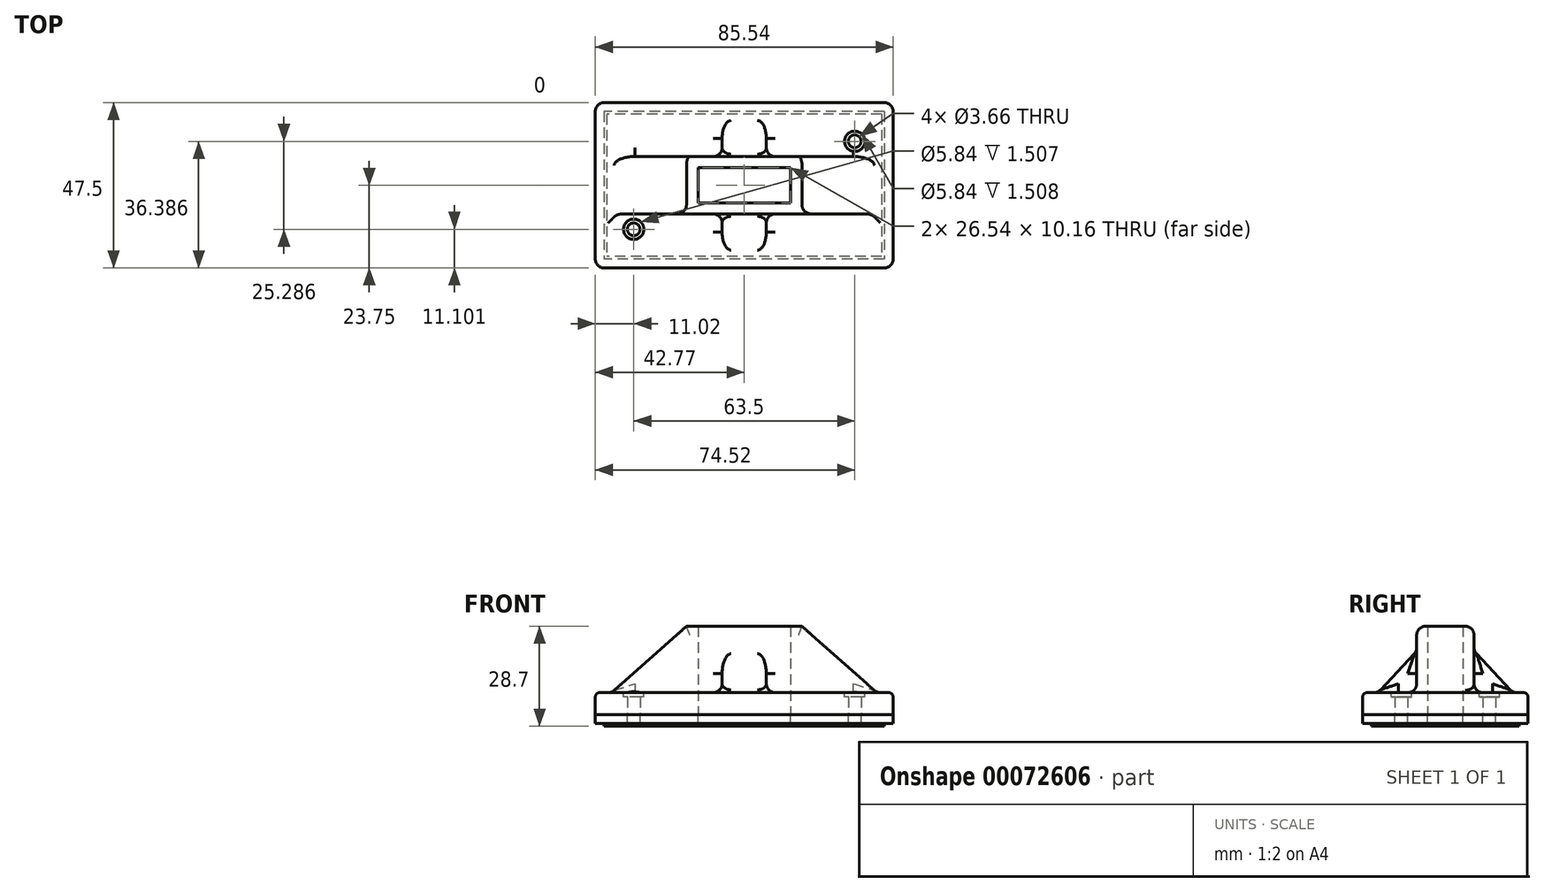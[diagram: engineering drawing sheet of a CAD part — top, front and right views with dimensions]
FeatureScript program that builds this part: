
annotation { "Feature Type Name" : "Feature", "Feature Type Description" : "" }
export const myFeature = defineFeature(function(context is Context, id is Id, definition is map)
    precondition{}
    {
        {
            var Q0;
            Q0=qCreatedBy(makeId("Top.planeOp"),FACE);
            var sketch = newSketch(context, id + "F0", { "sketchPlane" : qUnion([Q0])});
            skLineSegment(sketch, "E0.rect.bottom", {"start": v(42.77, 23.75) * mm, "end": v(-42.77, 23.75) * mm});
            skLineSegment(sketch, "E0.rect.top", {"start": v(42.77, -23.75) * mm, "end": v(-42.77, -23.75) * mm});
            skLineSegment(sketch, "E0.rect.left", {"start": v(42.77, 23.75) * mm, "end": v(42.77, -23.75) * mm});
            skLineSegment(sketch, "E0.rect.right", {"start": v(-42.77, 23.75) * mm, "end": v(-42.77, -23.75) * mm});
            skPoint(sketch, "E0.rect.middle", {"position": v(0, 0) * mm});
            skCircle(sketch, "E1", {"center": v(31.75, 12.64) * mm, "radius": 1.83 * mm});
            skCircle(sketch, "E2", {"center": v(-31.75, -12.65) * mm, "radius": 1.83 * mm});
            skSolve(sketch);
        }
        {
            var Q0;
            Q0 = qSketchRegion(id + "F0", true);
            extrude(context, id + "F1", {"entities" : qUnion([Q0]), "depth" : 6.35 * mm});
        }
        {
            var Q0;
            Q0=qCreatedBy(makeId("Top.planeOp"),FACE);
            var sketch = newSketch(context, id + "F2", { "sketchPlane" : qUnion([Q0])});
            skLineSegment(sketch, "E3.rect.bottom", {"start": v(38.1, -8.26) * mm, "end": v(-38.1, -8.26) * mm});
            skLineSegment(sketch, "E3.rect.top", {"start": v(38.1, 8.26) * mm, "end": v(-38.1, 8.26) * mm});
            skLineSegment(sketch, "E3.rect.left", {"start": v(38.1, -8.26) * mm, "end": v(38.1, 8.25) * mm});
            skLineSegment(sketch, "E3.rect.right", {"start": v(-38.1, -8.26) * mm, "end": v(-38.1, 8.25) * mm});
            skPoint(sketch, "E3.rect.middle", {"position": v(0, 0) * mm});
            skLineSegment(sketch, "E4.rect.bottom", {"start": v(13.27, -5.08) * mm, "end": v(-13.27, -5.08) * mm});
            skLineSegment(sketch, "E4.rect.top", {"start": v(13.27, 5.08) * mm, "end": v(-13.27, 5.08) * mm});
            skLineSegment(sketch, "E4.rect.left", {"start": v(13.27, -5.08) * mm, "end": v(13.27, 5.08) * mm});
            skLineSegment(sketch, "E4.rect.right", {"start": v(-13.27, -5.08) * mm, "end": v(-13.27, 5.08) * mm});
            skSolve(sketch);
        }
        {
            var Q0;
            Q0 = qSketchRegion(id + "F2", true);
            extrude(context, id + "F3", {"entities" : qUnion([Q0]), "operationType" : NewBodyOperationType.ADD, "depth" : 25.4 * mm});
        }
        {
            var Q0;
            Q0=makeQuery(id+"F3.opExtrude","SWEPT_FACE",FACE,{"disambiguationData":[OSD([sQuery(id+"F2.wireOp",EDGE,"E3.rect.bottom")])]});
            var sketch = newSketch(context, id + "F4", { "sketchPlane" : qUnion([Q0])});
            skPoint(sketch, "E5", {"position": v(16.6, 25.4) * mm});
            skPoint(sketch, "E6", {"position": v(-16.6, 25.4) * mm});
            skLineSegment(sketch, "E7", {"start": v(16.6, 25.4) * mm, "end": v(38.1, 6.35) * mm});
            skLineSegment(sketch, "E8", {"start": v(-16.6, 25.4) * mm, "end": v(-38.1, 6.35) * mm});
            skLineSegment(sketch, "E9", {"start": v(-16.6, 25.4) * mm, "end": v(16.6, 25.4) * mm});
            skLineSegment(sketch, "E10", {"start": v(38.1, 6.35) * mm, "end": v(-38.1, 6.35) * mm});
            skSolve(sketch);
        }
        {
            var Q0;
            {var subQ0=sQuery(id+"F4.wireOp",EDGE,"E7");Q0=makeQuery(id+"F4.imprint","IMPRINT",FACE,{"disambiguationData":[TD([[makeQuery(id+"F4.imprint","IMPRINT",EDGE,{"derivedFrom":subQ0}),1.0]])]});}
            extrude(context, id + "F5", {"entities" : qUnion([Q0]), "operationType" : NewBodyOperationType.REMOVE, "oppositeDirection" : true, "depth" : 44.81 * mm});
        }
        {
            var Q0;
            {var subQ0=sQuery(id+"F4.wireOp",EDGE,"E8");Q0=makeQuery(id+"F4.imprint","IMPRINT",FACE,{"disambiguationData":[TD([[makeQuery(id+"F4.imprint","IMPRINT",EDGE,{"derivedFrom":subQ0}),-1.0]])]});}
            extrude(context, id + "F6", {"entities" : qUnion([Q0]), "operationType" : NewBodyOperationType.REMOVE, "oppositeDirection" : true, "depth" : 25.4 * mm});
        }
        {
            var Q0;
            Q0=makeQuery(id+"F3.opExtrude","CAP_EDGE",EDGE,{"disambiguationData":[OSD([sQuery(id+"F2.wireOp",EDGE,"E3.rect.bottom")])],"isStart":false});
            var Q1;
            Q1=makeQuery(id+"F6.boolean.opBoolean","COPY",EDGE,{"derivedFrom":makeQuery(id+"F6.opExtrude","SWEPT_EDGE",EDGE,{"disambiguationData":[OSD([sQuery(id+"F2.wireOp",EDGE,"E3.rect.bottom"),sQuery(id+"F4.wireOp",EDGE,"E8"),sQuery(id+"F4.wireOp",EDGE,"E9")])]})});
            var Q2;
            Q2=makeQuery(id+"F3.opExtrude","CAP_EDGE",EDGE,{"disambiguationData":[OSD([sQuery(id+"F2.wireOp",EDGE,"E3.rect.top")])],"isStart":false});
            var Q3;
            Q3=makeQuery(id+"F5.boolean.opBoolean","COPY",EDGE,{"derivedFrom":makeQuery(id+"F5.opExtrude","SWEPT_EDGE",EDGE,{"disambiguationData":[OSD([sQuery(id+"F2.wireOp",EDGE,"E3.rect.bottom"),sQuery(id+"F4.wireOp",EDGE,"E7"),sQuery(id+"F4.wireOp",EDGE,"E9")])]})});
            var Q4;
            Q4=makeQuery(id+"F5.boolean.opBoolean","COPY",EDGE,{"derivedFrom":makeQuery(id+"F5.opExtrude","CAP_EDGE",EDGE,{"disambiguationData":[OSD([sQuery(id+"F4.wireOp",EDGE,"E7")])],"isStart":true})});
            var Q5;
            Q5=makeQuery(id+"F5.boolean.opBoolean","INTERSECT",EDGE,{"derivedFrom":[makeQuery(id+"F3.opExtrude","SWEPT_FACE",FACE,{"disambiguationData":[OSD([sQuery(id+"F2.wireOp",EDGE,"E3.rect.top")])]}),makeQuery(id+"F5.opExtrude","SWEPT_FACE",FACE,{"disambiguationData":[OSD([sQuery(id+"F4.wireOp",EDGE,"E7")])]})]});
            var Q6;
            Q6=makeQuery(id+"F6.boolean.opBoolean","COPY",EDGE,{"derivedFrom":makeQuery(id+"F6.opExtrude","CAP_EDGE",EDGE,{"disambiguationData":[OSD([sQuery(id+"F4.wireOp",EDGE,"E8")])],"isStart":true})});
            var Q7;
            Q7=makeQuery(id+"F6.boolean.opBoolean","INTERSECT",EDGE,{"derivedFrom":[makeQuery(id+"F3.opExtrude","SWEPT_FACE",FACE,{"disambiguationData":[OSD([sQuery(id+"F2.wireOp",EDGE,"E3.rect.top")])]}),makeQuery(id+"F6.opExtrude","SWEPT_FACE",FACE,{"disambiguationData":[OSD([sQuery(id+"F4.wireOp",EDGE,"E8")])]})]});
            var Q8;
            Q8=makeQuery(id+"F3.boolean.opBoolean","INTERSECT",EDGE,{"derivedFrom":[makeQuery(id+"F1.opExtrude","CAP_FACE",FACE,{"disambiguationData":[OSD([sQuery(id+"F0.wireOp",EDGE,"E0.rect.bottom"),sQuery(id+"F0.wireOp",EDGE,"E0.rect.top"),sQuery(id+"F0.wireOp",EDGE,"E0.rect.left"),sQuery(id+"F0.wireOp",EDGE,"E0.rect.right"),sQuery(id+"F0.wireOp",EDGE,"E1"),sQuery(id+"F0.wireOp",EDGE,"E2")])],"isStart":false}),makeQuery(id+"F3.opExtrude","SWEPT_FACE",FACE,{"disambiguationData":[OSD([sQuery(id+"F2.wireOp",EDGE,"E3.rect.bottom")])]})]});
            var Q9;
            Q9=makeQuery(id+"F3.boolean.opBoolean","INTERSECT",EDGE,{"derivedFrom":[makeQuery(id+"F1.opExtrude","CAP_FACE",FACE,{"disambiguationData":[OSD([sQuery(id+"F0.wireOp",EDGE,"E0.rect.bottom"),sQuery(id+"F0.wireOp",EDGE,"E0.rect.top"),sQuery(id+"F0.wireOp",EDGE,"E0.rect.left"),sQuery(id+"F0.wireOp",EDGE,"E0.rect.right"),sQuery(id+"F0.wireOp",EDGE,"E1"),sQuery(id+"F0.wireOp",EDGE,"E2")])],"isStart":false}),makeQuery(id+"F3.opExtrude","SWEPT_FACE",FACE,{"disambiguationData":[OSD([sQuery(id+"F2.wireOp",EDGE,"E3.rect.top")])]})]});
            var Q10;
            {var subQ0=sQuery(id+"F2.wireOp",EDGE,"E3.rect.right");Q10=makeQuery(id+"F6.boolean.opBoolean","MERGE",EDGE,{"derivedFrom":[makeQuery(id+"F3.boolean.opBoolean","INTERSECT",EDGE,{"derivedFrom":[makeQuery(id+"F1.opExtrude","CAP_FACE",FACE,{"disambiguationData":[OSD([sQuery(id+"F0.wireOp",EDGE,"E0.rect.bottom"),sQuery(id+"F0.wireOp",EDGE,"E0.rect.top"),sQuery(id+"F0.wireOp",EDGE,"E0.rect.left"),sQuery(id+"F0.wireOp",EDGE,"E0.rect.right"),sQuery(id+"F0.wireOp",EDGE,"E1"),sQuery(id+"F0.wireOp",EDGE,"E2")])],"isStart":false}),makeQuery(id+"F3.opExtrude","SWEPT_FACE",FACE,{"disambiguationData":[OSD([subQ0])]})]}),makeQuery(id+"F6.opExtrude","SWEPT_EDGE",EDGE,{"disambiguationData":[OSD([sQuery(id+"F2.wireOp",EDGE,"E3.rect.bottom"),subQ0,sQuery(id+"F4.wireOp",EDGE,"E8"),sQuery(id+"F4.wireOp",EDGE,"E10")])]})]});}
            var Q11;
            {var subQ0=sQuery(id+"F2.wireOp",EDGE,"E3.rect.left");Q11=makeQuery(id+"F5.boolean.opBoolean","MERGE",EDGE,{"derivedFrom":[makeQuery(id+"F3.boolean.opBoolean","INTERSECT",EDGE,{"derivedFrom":[makeQuery(id+"F1.opExtrude","CAP_FACE",FACE,{"disambiguationData":[OSD([sQuery(id+"F0.wireOp",EDGE,"E0.rect.bottom"),sQuery(id+"F0.wireOp",EDGE,"E0.rect.top"),sQuery(id+"F0.wireOp",EDGE,"E0.rect.left"),sQuery(id+"F0.wireOp",EDGE,"E0.rect.right"),sQuery(id+"F0.wireOp",EDGE,"E1"),sQuery(id+"F0.wireOp",EDGE,"E2")])],"isStart":false}),makeQuery(id+"F3.opExtrude","SWEPT_FACE",FACE,{"disambiguationData":[OSD([subQ0])]})]}),makeQuery(id+"F5.opExtrude","SWEPT_EDGE",EDGE,{"disambiguationData":[OSD([sQuery(id+"F2.wireOp",EDGE,"E3.rect.bottom"),subQ0,sQuery(id+"F4.wireOp",EDGE,"E7"),sQuery(id+"F4.wireOp",EDGE,"E10")])]})]});}
            fillet(context, id + "F7", {"entities" : qUnion([Q0, Q1, Q2, Q3, Q4, Q5, Q6, Q7, Q8, Q9, Q10, Q11]), "radius" : 2.54 * mm, "tangentPropagation" : true, "allowEdgeOverflow" : false});
        }
        {
            var Q0;
            Q0=makeQuery(id+"F1.opExtrude","CAP_EDGE",EDGE,{"disambiguationData":[OSD([sQuery(id+"F0.wireOp",EDGE,"E0.rect.top")])],"isStart":false});
            var Q1;
            Q1=makeQuery(id+"F1.opExtrude","CAP_EDGE",EDGE,{"disambiguationData":[OSD([sQuery(id+"F0.wireOp",EDGE,"E0.rect.right")])],"isStart":false});
            var Q2;
            Q2=makeQuery(id+"F1.opExtrude","CAP_EDGE",EDGE,{"disambiguationData":[OSD([sQuery(id+"F0.wireOp",EDGE,"E0.rect.bottom")])],"isStart":false});
            var Q3;
            Q3=makeQuery(id+"F1.opExtrude","CAP_EDGE",EDGE,{"disambiguationData":[OSD([sQuery(id+"F0.wireOp",EDGE,"E0.rect.left")])],"isStart":false});
            fillet(context, id + "F8", {"entities" : qUnion([Q0, Q1, Q2, Q3]), "radius" : 1.27 * mm, "tangentPropagation" : true, "allowEdgeOverflow" : false});
        }
        {
            var Q0;
            Q0=makeQuery(id+"F1.opExtrude","SWEPT_EDGE",EDGE,{"disambiguationData":[OSD([sQuery(id+"F0.wireOp",EDGE,"E0.rect.bottom"),sQuery(id+"F0.wireOp",EDGE,"E0.rect.left")])]});
            var Q1;
            Q1=makeQuery(id+"F1.opExtrude","SWEPT_EDGE",EDGE,{"disambiguationData":[OSD([sQuery(id+"F0.wireOp",EDGE,"E0.rect.bottom"),sQuery(id+"F0.wireOp",EDGE,"E0.rect.right")])]});
            var Q2;
            Q2=makeQuery(id+"F1.opExtrude","SWEPT_EDGE",EDGE,{"disambiguationData":[OSD([sQuery(id+"F0.wireOp",EDGE,"E0.rect.top"),sQuery(id+"F0.wireOp",EDGE,"E0.rect.right")])]});
            var Q3;
            Q3=makeQuery(id+"F1.opExtrude","SWEPT_EDGE",EDGE,{"disambiguationData":[OSD([sQuery(id+"F0.wireOp",EDGE,"E0.rect.top"),sQuery(id+"F0.wireOp",EDGE,"E0.rect.left")])]});
            fillet(context, id + "F9", {"entities" : qUnion([Q0, Q1, Q2, Q3]), "radius" : 2.54 * mm, "tangentPropagation" : true, "allowEdgeOverflow" : false});
        }
        {
            var Q0;
            {var subQ0=sQuery(id+"F0.wireOp",EDGE,"E0.rect.right");var subQ1=sQuery(id+"F0.wireOp",EDGE,"E0.rect.left");var subQ2=sQuery(id+"F0.wireOp",EDGE,"E0.rect.top");var subQ3=sQuery(id+"F0.wireOp",EDGE,"E0.rect.bottom");var subQ4=sQuery(id+"F0.wireOp",EDGE,"E1");var subQ5=sQuery(id+"F0.wireOp",EDGE,"E2");Q0=makeQuery(id+"F3.boolean.opBoolean","SPLIT",FACE,{"disambiguationData":[TD([makeQuery(id+"F1.opExtrude","SWEPT_FACE",FACE,{"disambiguationData":[OSD([subQ3])]})])],"derivedFrom":makeQuery(id+"F1.opExtrude","CAP_FACE",FACE,{"disambiguationData":[OSD([subQ3,subQ2,subQ1,subQ0,subQ4,subQ5])],"isStart":false})});}
            var sketch = newSketch(context, id + "F10", { "sketchPlane" : qUnion([Q0])});
            skCircle(sketch, "E11", {"center": v(31.75, 12.64) * mm, "radius": 2.92 * mm});
            skCircle(sketch, "E12", {"center": v(-31.75, -12.65) * mm, "radius": 2.92 * mm});
            skSolve(sketch);
        }
        {
            var Q0;
            Q0 = qSketchRegion(id + "F10", true);
            extrude(context, id + "F11", {"entities" : qUnion([Q0]), "operationType" : NewBodyOperationType.REMOVE, "endBound" : BoundingType.SYMMETRIC, "oppositeDirection" : true, "depth" : 2.54 * mm});
        }
        {
            var Q0;
            Q0=qCreatedBy(makeId("Top.planeOp"),FACE);
            var sketch = newSketch(context, id + "F12", { "sketchPlane" : qUnion([Q0])});
            skLineSegment(sketch, "E13.rect.bottom", {"start": v(13.27, -5.08) * mm, "end": v(-13.27, -5.08) * mm});
            skLineSegment(sketch, "E13.rect.top", {"start": v(13.27, 5.08) * mm, "end": v(-13.27, 5.08) * mm});
            skLineSegment(sketch, "E13.rect.left", {"start": v(13.27, -5.08) * mm, "end": v(13.27, 5.08) * mm});
            skLineSegment(sketch, "E13.rect.right", {"start": v(-13.27, -5.08) * mm, "end": v(-13.27, 5.08) * mm});
            skPoint(sketch, "E13.rect.middle", {"position": v(0, 0) * mm});
            skSolve(sketch);
        }
        {
            var Q0;
            Q0 = qSketchRegion(id + "F12", true);
            extrude(context, id + "F13", {"entities" : qUnion([Q0]), "operationType" : NewBodyOperationType.REMOVE, "depth" : 25.4 * mm});
        }
        {
            var Q0;
            Q0=qCreatedBy(makeId("Right.planeOp"),FACE);
            var sketch = newSketch(context, id + "F14", { "sketchPlane" : qUnion([Q0])});
            skLineSegment(sketch, "E14", {"start": v(7.87, 18.64) * mm, "end": v(19.7, 6) * mm});
            skLineSegment(sketch, "E15", {"start": v(19.7, 6) * mm, "end": v(7.62, 6) * mm});
            skLineSegment(sketch, "E16", {"start": v(7.62, 6) * mm, "end": v(7.87, 18.64) * mm});
            skLineSegment(sketch, "E17.MirrorCS", {"start": v(-7.87, 18.64) * mm, "end": v(-19.7, 6) * mm});
            skLineSegment(sketch, "E18.MirrorCS", {"start": v(-7.62, 6) * mm, "end": v(-7.87, 18.64) * mm});
            skLineSegment(sketch, "E19.MirrorCS", {"start": v(-19.7, 6) * mm, "end": v(-7.62, 6) * mm});
            skSolve(sketch);
        }
        {
            var Q0;
            Q0 = qSketchRegion(id + "F14", true);
            extrude(context, id + "F15", {"entities" : qUnion([Q0]), "operationType" : NewBodyOperationType.ADD, "endBound" : BoundingType.SYMMETRIC, "depth" : 12.7 * mm});
        }
        {
            var Q0;
            Q0=makeQuery(id+"F15.boolean.opBoolean","INTERSECT",EDGE,{"derivedFrom":[makeQuery(id+"F3.opExtrude","SWEPT_FACE",FACE,{"disambiguationData":[OSD([sQuery(id+"F2.wireOp",EDGE,"E3.rect.bottom")])]}),makeQuery(id+"F15.opExtrude","SWEPT_FACE",FACE,{"disambiguationData":[OSD([sQuery(id+"F14.wireOp",EDGE,"E17.MirrorCS")])]})]});
            var Q1;
            Q1=makeQuery(id+"F15.opExtrude","CAP_EDGE",EDGE,{"disambiguationData":[OSD([sQuery(id+"F14.wireOp",EDGE,"E17.MirrorCS")])],"isStart":true});
            var Q2;
            Q2=makeQuery(id+"F15.opExtrude","CAP_EDGE",EDGE,{"disambiguationData":[OSD([sQuery(id+"F14.wireOp",EDGE,"E17.MirrorCS")])],"isStart":false});
            var Q3;
            {var subQ0=sQuery(id+"F0.wireOp",EDGE,"E0.rect.right");var subQ1=sQuery(id+"F0.wireOp",EDGE,"E0.rect.left");var subQ2=sQuery(id+"F0.wireOp",EDGE,"E0.rect.top");var subQ3=sQuery(id+"F0.wireOp",EDGE,"E0.rect.bottom");var subQ4=sQuery(id+"F0.wireOp",EDGE,"E1");var subQ5=sQuery(id+"F0.wireOp",EDGE,"E2");Q3=makeQuery(id+"F15.boolean.opBoolean","INTERSECT",EDGE,{"derivedFrom":[makeQuery(id+"F3.boolean.opBoolean","SPLIT",FACE,{"disambiguationData":[TD([makeQuery(id+"F1.opExtrude","SWEPT_FACE",FACE,{"disambiguationData":[OSD([subQ3])]})])],"derivedFrom":makeQuery(id+"F1.opExtrude","CAP_FACE",FACE,{"disambiguationData":[OSD([subQ3,subQ2,subQ1,subQ0,subQ4,subQ5])],"isStart":false})}),makeQuery(id+"F15.opExtrude","SWEPT_FACE",FACE,{"disambiguationData":[OSD([sQuery(id+"F14.wireOp",EDGE,"E17.MirrorCS")])]})]});}
            var Q4;
            Q4=makeQuery(id+"F15.opExtrude","CAP_FACE",FACE,{"disambiguationData":[OSD([sQuery(id+"F14.wireOp",EDGE,"E17.MirrorCS"),sQuery(id+"F14.wireOp",EDGE,"E18.MirrorCS"),sQuery(id+"F14.wireOp",EDGE,"E19.MirrorCS")])],"isStart":true});
            var Q5;
            Q5=makeQuery(id+"F15.opExtrude","CAP_FACE",FACE,{"disambiguationData":[OSD([sQuery(id+"F14.wireOp",EDGE,"E17.MirrorCS"),sQuery(id+"F14.wireOp",EDGE,"E18.MirrorCS"),sQuery(id+"F14.wireOp",EDGE,"E19.MirrorCS")])],"isStart":false});
            fillet(context, id + "F16", {"entities" : qUnion([Q0, Q1, Q2, Q3, Q4, Q5]), "radius" : 2.54 * mm, "tangentPropagation" : true, "allowEdgeOverflow" : false});
        }
        {
            var Q0;
            Q0=makeQuery(id+"F15.boolean.opBoolean","INTERSECT",EDGE,{"derivedFrom":[makeQuery(id+"F3.opExtrude","SWEPT_FACE",FACE,{"disambiguationData":[OSD([sQuery(id+"F2.wireOp",EDGE,"E3.rect.top")])]}),makeQuery(id+"F15.opExtrude","SWEPT_FACE",FACE,{"disambiguationData":[OSD([sQuery(id+"F14.wireOp",EDGE,"E14")])]})]});
            var Q1;
            Q1=makeQuery(id+"F15.opExtrude","CAP_EDGE",EDGE,{"disambiguationData":[OSD([sQuery(id+"F14.wireOp",EDGE,"E14")])],"isStart":true});
            var Q2;
            {var subQ0=sQuery(id+"F0.wireOp",EDGE,"E0.rect.right");var subQ1=sQuery(id+"F0.wireOp",EDGE,"E0.rect.left");var subQ2=sQuery(id+"F0.wireOp",EDGE,"E0.rect.top");var subQ3=sQuery(id+"F0.wireOp",EDGE,"E0.rect.bottom");var subQ4=sQuery(id+"F0.wireOp",EDGE,"E1");var subQ5=sQuery(id+"F0.wireOp",EDGE,"E2");Q2=makeQuery(id+"F15.boolean.opBoolean","INTERSECT",EDGE,{"derivedFrom":[makeQuery(id+"F3.boolean.opBoolean","SPLIT",FACE,{"disambiguationData":[TD([makeQuery(id+"F1.opExtrude","SWEPT_FACE",FACE,{"disambiguationData":[OSD([subQ3])]})])],"derivedFrom":makeQuery(id+"F1.opExtrude","CAP_FACE",FACE,{"disambiguationData":[OSD([subQ3,subQ2,subQ1,subQ0,subQ4,subQ5])],"isStart":false})}),makeQuery(id+"F15.opExtrude","SWEPT_FACE",FACE,{"disambiguationData":[OSD([sQuery(id+"F14.wireOp",EDGE,"E14")])]})]});}
            var Q3;
            Q3=makeQuery(id+"F15.opExtrude","CAP_EDGE",EDGE,{"disambiguationData":[OSD([sQuery(id+"F14.wireOp",EDGE,"E14")])],"isStart":false});
            var Q4;
            Q4=makeQuery(id+"F15.opExtrude","CAP_FACE",FACE,{"disambiguationData":[OSD([sQuery(id+"F14.wireOp",EDGE,"E14"),sQuery(id+"F14.wireOp",EDGE,"E15"),sQuery(id+"F14.wireOp",EDGE,"E16")])],"isStart":false});
            var Q5;
            Q5=makeQuery(id+"F15.opExtrude","CAP_FACE",FACE,{"disambiguationData":[OSD([sQuery(id+"F14.wireOp",EDGE,"E14"),sQuery(id+"F14.wireOp",EDGE,"E15"),sQuery(id+"F14.wireOp",EDGE,"E16")])],"isStart":true});
            fillet(context, id + "F17", {"entities" : qUnion([Q0, Q1, Q2, Q3, Q4, Q5]), "radius" : 2.54 * mm, "tangentPropagation" : true, "allowEdgeOverflow" : false});
        }
        {
            var Q0;
            Q0=qCreatedBy(makeId("Top.planeOp"),FACE);
            var sketch = newSketch(context, id + "F18", { "sketchPlane" : qUnion([Q0])});
            skLineSegment(sketch, "E20.0", {"start": v(40.23, -23.75) * mm, "end": v(-40.23, -23.75) * mm});
            skPoint(sketch, "E21.0", {"position": v(42.77, -21.2) * mm});
            skLineSegment(sketch, "E22.0", {"start": v(42.77, 21.2) * mm, "end": v(42.77, -21.2) * mm});
            skArc(sketch, "E23.0", {"start": v(40.23, 23.75) * mm, "mid": v(42.03, 23) * mm, "end": v(42.77, 21.2) * mm});
            skLineSegment(sketch, "E24.0", {"start": v(40.23, 23.75) * mm, "end": v(-40.23, 23.75) * mm});
            skArc(sketch, "E25.0", {"start": v(-42.77, 21.2) * mm, "mid": v(-42.03, 23) * mm, "end": v(-40.23, 23.75) * mm});
            skLineSegment(sketch, "E26.0", {"start": v(-42.77, 21.2) * mm, "end": v(-42.77, -21.2) * mm});
            skArc(sketch, "E27.0", {"start": v(-40.23, -23.75) * mm, "mid": v(-42.03, -23) * mm, "end": v(-42.77, -21.2) * mm});
            skCircle(sketch, "E28.0", {"center": v(-31.75, -12.65) * mm, "radius": 1.83 * mm});
            skCircle(sketch, "E29.0", {"center": v(31.75, 12.64) * mm, "radius": 1.83 * mm});
            skLineSegment(sketch, "E30.0", {"start": v(13.27, -5.08) * mm, "end": v(13.27, 5.08) * mm});
            skLineSegment(sketch, "E31.0", {"start": v(13.27, -5.08) * mm, "end": v(-13.27, -5.08) * mm});
            skLineSegment(sketch, "E32.0", {"start": v(-13.27, -5.08) * mm, "end": v(-13.27, 5.08) * mm});
            skLineSegment(sketch, "E33.0", {"start": v(13.27, 5.08) * mm, "end": v(-13.27, 5.08) * mm});
            skArc(sketch, "E34.0", {"start": v(42.77, -21.2) * mm, "mid": v(42.03, -23) * mm, "end": v(40.23, -23.75) * mm});
            skSolve(sketch);
        }
        {
            var Q0;
            Q0 = qSketchRegion(id + "F18", true);
            extrude(context, id + "F19", {"entities" : qUnion([Q0]), "oppositeDirection" : true, "depth" : 2.54 * mm});
        }
        {
            var Q0;
            Q0=makeQuery(id+"F19.opExtrude","CAP_FACE",FACE,{"disambiguationData":[OSD([sQuery(id+"F18.wireOp",EDGE,"E20.0"),sQuery(id+"F18.wireOp",EDGE,"E22.0"),sQuery(id+"F18.wireOp",EDGE,"E23.0"),sQuery(id+"F18.wireOp",EDGE,"E24.0"),sQuery(id+"F18.wireOp",EDGE,"E25.0"),sQuery(id+"F18.wireOp",EDGE,"E26.0"),sQuery(id+"F18.wireOp",EDGE,"E27.0"),sQuery(id+"F18.wireOp",EDGE,"E28.0"),sQuery(id+"F18.wireOp",EDGE,"E29.0"),sQuery(id+"F18.wireOp",EDGE,"E30.0"),sQuery(id+"F18.wireOp",EDGE,"E31.0"),sQuery(id+"F18.wireOp",EDGE,"E32.0"),sQuery(id+"F18.wireOp",EDGE,"E33.0"),sQuery(id+"F18.wireOp",EDGE,"E34.0")])],"isStart":false});
            var sketch = newSketch(context, id + "F20", { "sketchPlane" : qUnion([Q0])});
            skLineSegment(sketch, "E35.0", {"start": v(-40.23, 21.2) * mm, "end": v(-40.23, 21.2) * mm});
            skLineSegment(sketch, "E36.0", {"start": v(40.23, 21.2) * mm, "end": v(-40.23, 21.2) * mm});
            skLineSegment(sketch, "E37.0", {"start": v(40.23, -21.2) * mm, "end": v(40.23, 21.2) * mm});
            skLineSegment(sketch, "E38.0", {"start": v(40.23, -21.2) * mm, "end": v(-40.23, -21.2) * mm});
            skLineSegment(sketch, "E39.0", {"start": v(-40.23, -21.2) * mm, "end": v(-40.23, 21.2) * mm});
            skLineSegment(sketch, "E40.0", {"start": v(39.47, 20.45) * mm, "end": v(-39.47, 20.45) * mm});
            skLineSegment(sketch, "E40.1", {"start": v(39.47, -20.45) * mm, "end": v(39.47, 20.45) * mm});
            skLineSegment(sketch, "E40.2", {"start": v(39.47, -20.45) * mm, "end": v(-39.47, -20.45) * mm});
            skLineSegment(sketch, "E40.3", {"start": v(-39.47, -20.45) * mm, "end": v(-39.47, 20.45) * mm});
            skSolve(sketch);
        }
        {
            var Q0;
            Q0=makeQuery(id+"F20.imprint","IMPRINT",FACE,{"disambiguationData":[TD([[makeQuery(id+"F20.imprint","IMPRINT",EDGE,{"derivedFrom":sQuery(id+"F20.wireOp",EDGE,"E36.0")}),1.0]])]});
            extrude(context, id + "F21", {"entities" : qUnion([Q0]), "operationType" : NewBodyOperationType.ADD, "depth" : 0.76 * mm});
        }
    });
